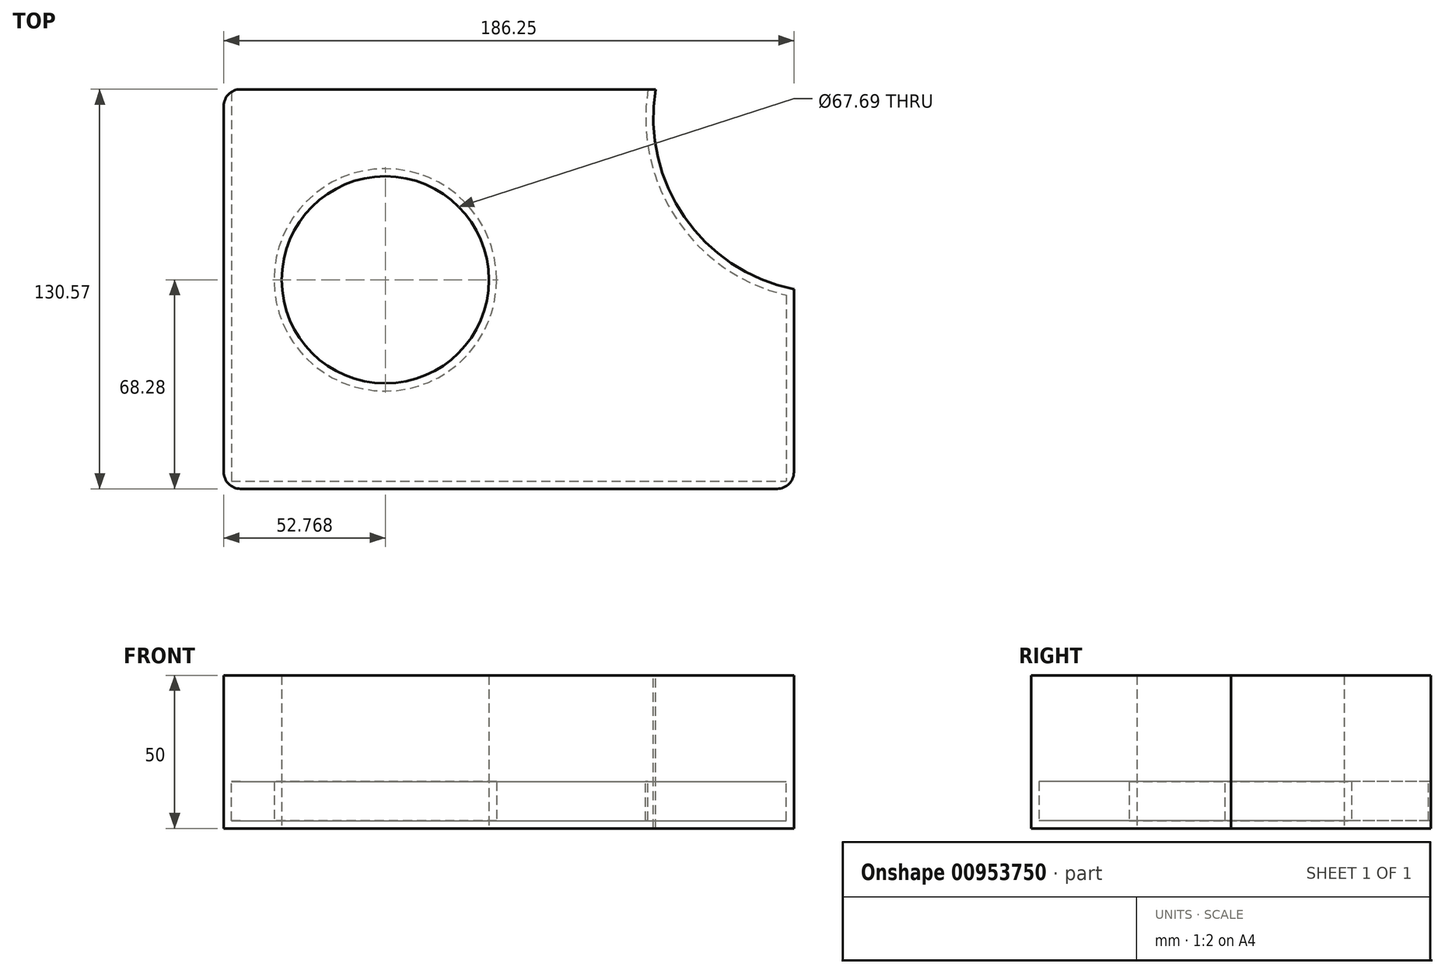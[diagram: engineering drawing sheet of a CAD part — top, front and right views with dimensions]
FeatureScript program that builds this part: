
annotation { "Feature Type Name" : "Feature", "Feature Type Description" : "" }
export const myFeature = defineFeature(function(context is Context, id is Id, definition is map)
    precondition{}
    {
        {
            var Q0;
            Q0=qCreatedBy(makeId("Top.planeOp"),FACE);
            var sketch = newSketch(context, id + "F0", { "sketchPlane" : qUnion([Q0])});
            skLineSegment(sketch, "E0.bottom", {"start": v(-97.53, 62.29) * mm, "end": v(88.72, 62.29) * mm});
            skLineSegment(sketch, "E0.top", {"start": v(-97.53, -68.28) * mm, "end": v(88.72, -68.28) * mm});
            skLineSegment(sketch, "E0.left", {"start": v(-97.53, 62.29) * mm, "end": v(-97.53, -68.28) * mm});
            skLineSegment(sketch, "E0.right", {"start": v(88.72, 62.29) * mm, "end": v(88.72, -68.28) * mm});
            skSolve(sketch);
        }
        {
            var Q0;
            Q0 = qSketchRegion(id + "F0", true);
            extrude(context, id + "F1", {"entities" : qUnion([Q0]), "depth" : 50 * mm, "offsetDistance" : 25 * mm});
        }
        {
            var Q0;
            Q0=makeQuery(id+"F1.opExtrude","CAP_FACE",FACE,{"disambiguationData":[OSD([sQuery(id+"F0.wireOp",EDGE,"E0.bottom"),sQuery(id+"F0.wireOp",EDGE,"E0.top"),sQuery(id+"F0.wireOp",EDGE,"E0.left"),sQuery(id+"F0.wireOp",EDGE,"E0.right")])],"isStart":true});
            var sketch = newSketch(context, id + "F2", { "sketchPlane" : qUnion([Q0])});
            skCircle(sketch, "E1", {"center": v(-44.76, 0) * mm, "radius": 33.84 * mm});
            skSolve(sketch);
        }
        {
            var Q0;
            Q0=makeQuery(id+"F2.imprint","IMPRINT",FACE,{"disambiguationData":[TD([[makeQuery(id+"F2.imprint","IMPRINT",EDGE,{"derivedFrom":sQuery(id+"F2.wireOp",EDGE,"E1")}),1.0]])]});
            extrude(context, id + "F3", {"entities" : qUnion([Q0]), "operationType" : NewBodyOperationType.REMOVE, "oppositeDirection" : true, "depth" : 153 * mm, "offsetDistance" : 25 * mm});
        }
        {
            var Q0;
            Q0=makeQuery(id+"F1.opExtrude","CAP_FACE",FACE,{"disambiguationData":[OSD([sQuery(id+"F0.wireOp",EDGE,"E0.bottom"),sQuery(id+"F0.wireOp",EDGE,"E0.top"),sQuery(id+"F0.wireOp",EDGE,"E0.left"),sQuery(id+"F0.wireOp",EDGE,"E0.right")])],"isStart":false});
            var sketch = newSketch(context, id + "F4", { "sketchPlane" : qUnion([Q0])});
            skArc(sketch, "E2", {"start": v(43.56, 62.29) * mm, "mid": v(52.94, 20.52) * mm, "end": v(88.72, -3) * mm});
            skSolve(sketch);
        }
        {
            var Q0;
            Q0 = qSketchRegion(id + "F4", true);
            var Q1;
            {var subQ0=sQuery(id+"F4.wireOp",EDGE,"E2");Q1=makeQuery(id+"F4.imprint","IMPRINT",FACE,{"disambiguationData":[TD([[makeQuery(id+"F4.imprint","IMPRINT",EDGE,{"derivedFrom":subQ0}),1.0]])]});}
            extrude(context, id + "F5", {"entities" : qUnion([Q0, Q1]), "operationType" : NewBodyOperationType.REMOVE, "oppositeDirection" : true, "depth" : 98 * mm, "offsetDistance" : 25 * mm});
        }
        {
            var Q0;
            Q0=makeQuery(id+"F1.opExtrude","SWEPT_FACE",FACE,{"disambiguationData":[OSD([sQuery(id+"F0.wireOp",EDGE,"E0.bottom")])]});
            shell(context, id + "F6", {"entities" : qUnion([Q0]), "thickness" : 2.5 * mm});
        }
        {
            var Q0;
            Q0=makeQuery(id+"F1.opExtrude","CAP_FACE",FACE,{"disambiguationData":[OSD([sQuery(id+"F0.wireOp",EDGE,"E0.bottom"),sQuery(id+"F0.wireOp",EDGE,"E0.top"),sQuery(id+"F0.wireOp",EDGE,"E0.left"),sQuery(id+"F0.wireOp",EDGE,"E0.right")])],"isStart":false});
            extrude(context, id + "F7", {"entities" : qUnion([Q0]), "operationType" : NewBodyOperationType.ADD, "oppositeDirection" : true, "depth" : 34.7 * mm, "offsetDistance" : 25 * mm});
        }
        {
            var Q0;
            Q0=makeQuery(id+"F1.opExtrude","SWEPT_EDGE",EDGE,{"disambiguationData":[OSD([sQuery(id+"F0.wireOp",EDGE,"E0.top"),sQuery(id+"F0.wireOp",EDGE,"E0.left")])]});
            var Q1;
            Q1=makeQuery(id+"F1.opExtrude","SWEPT_EDGE",EDGE,{"disambiguationData":[OSD([sQuery(id+"F0.wireOp",EDGE,"E0.top"),sQuery(id+"F0.wireOp",EDGE,"E0.right")])]});
            var Q2;
            Q2=makeQuery(id+"F1.opExtrude","SWEPT_EDGE",EDGE,{"disambiguationData":[OSD([sQuery(id+"F0.wireOp",EDGE,"E0.bottom"),sQuery(id+"F0.wireOp",EDGE,"E0.left")])]});
            var Q3;
            Q3=makeQuery(id+"F5.boolean.opBoolean","COPY",EDGE,{"derivedFrom":makeQuery(id+"F5.opExtrude","SWEPT_EDGE",EDGE,{"disambiguationData":[OSD([sQuery(id+"F0.wireOp",EDGE,"E0.bottom"),sQuery(id+"F4.wireOp",EDGE,"E2")])]})});
            var Q4;
            Q4=makeQuery(id+"F5.boolean.opBoolean","COPY",EDGE,{"derivedFrom":makeQuery(id+"F5.opExtrude","SWEPT_EDGE",EDGE,{"disambiguationData":[OSD([sQuery(id+"F0.wireOp",EDGE,"E0.right"),sQuery(id+"F4.wireOp",EDGE,"E2")])]})});
            fillet(context, id + "F8", {"entities" : qUnion([Q0, Q1, Q2, Q3, Q4]), "tangentPropagation" : true, "radius" : 5.46 * mm, "defaultsChanged" : true, "vertexSettings" : [], "allowEdgeOverflow" : false});
        }
    });
